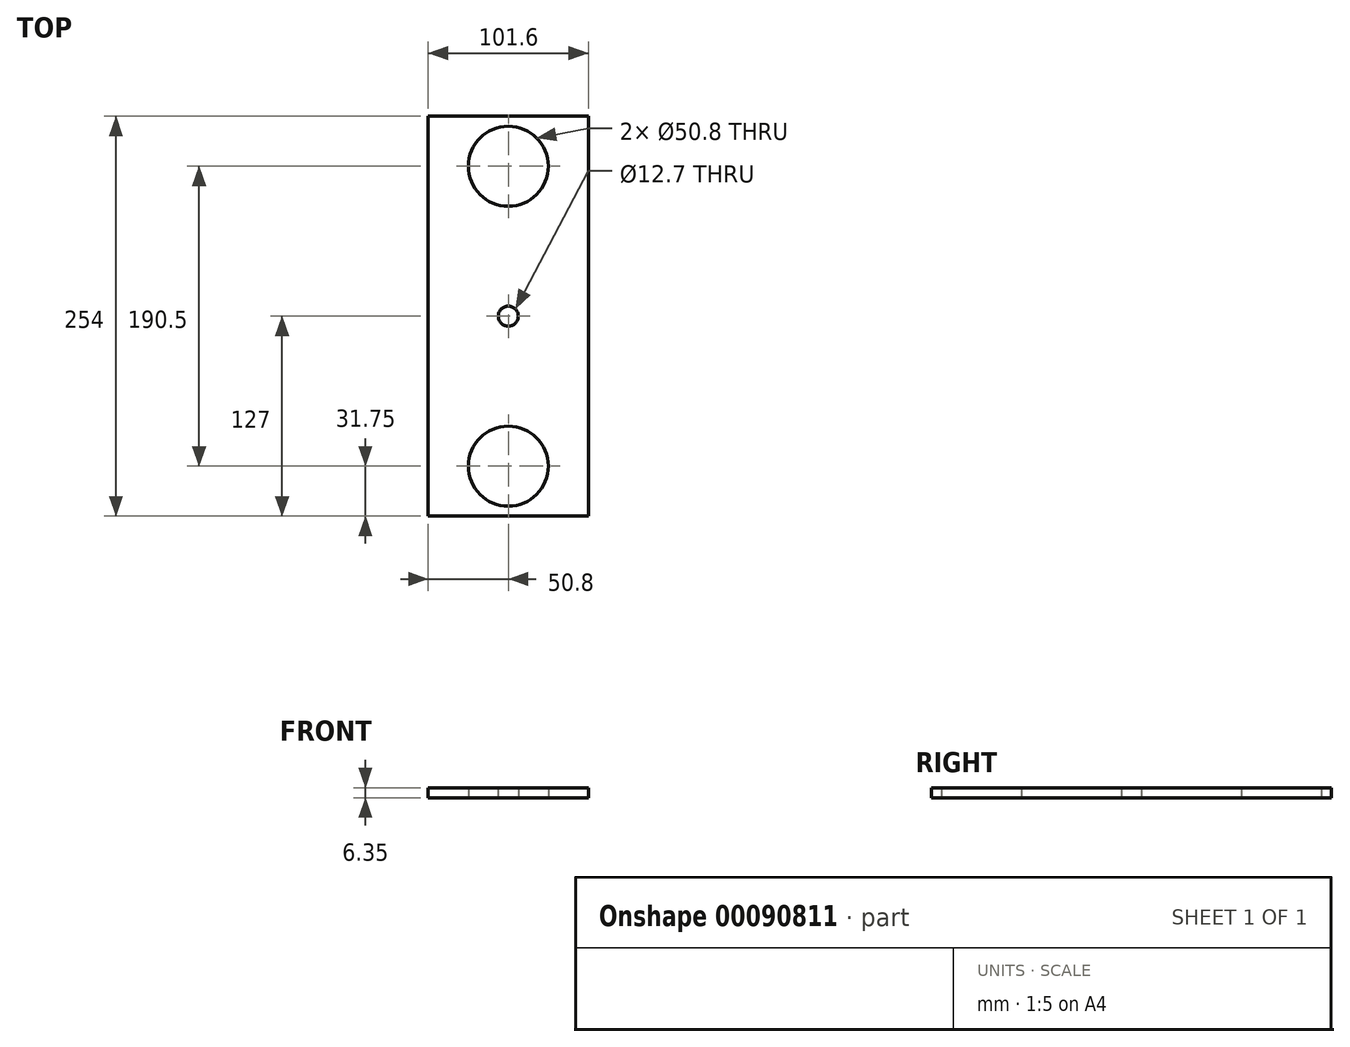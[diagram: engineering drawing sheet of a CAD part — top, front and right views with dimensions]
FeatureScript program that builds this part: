
annotation { "Feature Type Name" : "Feature", "Feature Type Description" : "" }
export const myFeature = defineFeature(function(context is Context, id is Id, definition is map)
    precondition{}
    {
        {
            var Q0;
            Q0=qCreatedBy(makeId("Top.planeOp"),FACE);
            var sketch = newSketch(context, id + "F0", { "sketchPlane" : qUnion([Q0])});
            skLineSegment(sketch, "E0.bottom", {"start": v(-50.8, 0) * mm, "end": v(50.8, 0) * mm});
            skLineSegment(sketch, "E0.top", {"start": v(-50.8, -254) * mm, "end": v(50.8, -254) * mm});
            skLineSegment(sketch, "E0.left", {"start": v(-50.8, 0) * mm, "end": v(-50.8, -254) * mm});
            skLineSegment(sketch, "E0.right", {"start": v(50.8, 0) * mm, "end": v(50.8, -254) * mm});
            skPoint(sketch, "E1", {"position": v(0, 0) * mm});
            skCircle(sketch, "E2", {"center": v(0, -31.75) * mm, "radius": 25.4 * mm});
            skCircle(sketch, "E3", {"center": v(0, -222.25) * mm, "radius": 25.4 * mm});
            skCircle(sketch, "E4", {"center": v(0, -127) * mm, "radius": 6.35 * mm});
            skPoint(sketch, "E4.centerSnap0", {"position": v(-50.8, -127) * mm});
            skSolve(sketch);
        }
        {
            var Q0;
            Q0 = qSketchRegion(id + "F0", true);
            extrude(context, id + "F1", {"entities" : qUnion([Q0]), "depth" : 6.35 * mm});
        }
    });
